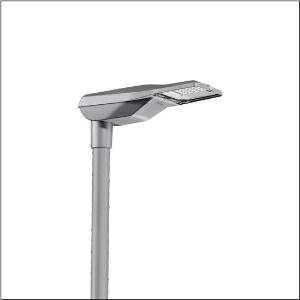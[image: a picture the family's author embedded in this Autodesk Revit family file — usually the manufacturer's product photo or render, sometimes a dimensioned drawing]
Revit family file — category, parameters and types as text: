
# Revit family: streetlight_sl_21_iq_micro___st1_0a_5xe1d41g08cb_d625
name_source: partatom
category: Lighting Fixtures
units: mm (PartAtom-declared; Revit-internal decimal feet)

## family parameters
Cut with Voids When Loaded = No
Host = Face
Light Source = No
Part Type = Normal
Room Calculation Point = No
Round Connector Dimension = Use Diameter
Shared = No

## types (1)
- --- (1 x LED, 2980 lm, 19.4 W, 4000K)
    Apparent Load = 19 VA
    CIE Flux Codes = 37 72 97 100 100
    Color Rendering = 70
    Color Temperature = 4000K
    Default Elevation = 1800 mm
    Description = Streetlight SL 21 iQ micro, mast luminaire, primary light control with lens, of PMMA, primary optical cover: cover, of toughened safety glass, transparent, light distribution: ST1.0a, light emission: direct distribution, primary light characteristic: asymmetric, installation type: post-top, side-entry, LED, High Power LED, rated luminous flux: 2.980lm, luminous efficacy: 154lm/W, light colour: 740, colour temperature: 4000K, control: Street-Remote, Auto-Match, Temp-Guard, Lumen-Switch, Night-Set, Smart-Wire, Light-Fading, Desk-Remote (wireless, voltage-free reading and setting of iQ features in the workshop via application-optimized NFC function/RFID function), optimised constant luminous flux control (CLO 2.0), presetting dimming linear, mains connection: 220..240V, AC, 50/60Hz, start of lifetime: 19W, end of service life: 20W, reduction: 10W, luminaire housing, of diecast aluminium, powder-coated, Siteco® metallic grey (DB 702S), corrosivity category C5 mid according to DIN EN ISO 12944, please order mast flange separately, inclination adjustable: 0°, 5°, 10°, 15°, sealing non-destructively replaceable, multi-level sealing system, length: 528mm, width: 235mm, height: 110mm, mast flange for spigot size: 42mm (side-entry): 5XC10008XM4, 60/48mm (side-entry/post-top): 5XC10108XM2, 76/60mm (side-entry/post-top): 5XC10108XM1, protection rating (complete): IP66, insulation class (complete): insulation class II (safety insulation), certification: CE, ENEC, ENEC+, VDE, impact resistance: IK09, permissible operating ambient temperature for outdoor applications: -40..+50°C, standard-compliant lighting for roads and squares, packaging unit: 1 piece

Light Distribution: ST1.0a
    Height = 110 mm
    Lamp = 1 x LED
    Lamp Light Flux = 2980 lm
    Lamp Power = 19.4 W
    Lamp count = 1
    Length = 528 mm
    Luminous efficacy = 154 lm/W
    Manufacturer = Siteco
    ModVariant = No
    Model = 5XE1D41G08CB
    Number of Poles = 1
    OnlyDefault = Yes
    Power Factor = 1
    Product Name = Streetlight SL 21 iQ micro | ST1.0a
    Product group = mast luminaire | pylon top
    ProductGroupID = 6100
    Protection Class = Protection class II
    Protection Degree = IP 66
    RLX_Detail_Level = 1
    RLX_Emergency_Light_Flux = 0 lm
    RLX_Emergency_Type = 0
    RLX_Emergency_Type_DB = No
    RlxData = <blob elided: 98805 chars, md5=195e1832>
    Socket = socket
    Standby Power = 0 W
    System Light Flux = 2980 lm
    System Power = 19 W
    Type Comments = factory setting: luminous flux: 100 % | dim-lin: 254 | 387 mA
    Type Image = l_1006881.jpg
    URL = http://relux.com
    VarID = @adj_088549
    Voltage = 0 V
    Weight = 0.00 kg
    Width = 235 mm

## geometry (parser evidence)
native form markers: Blend x4, Sweep x11
no freeform markers — native parametric forms only
